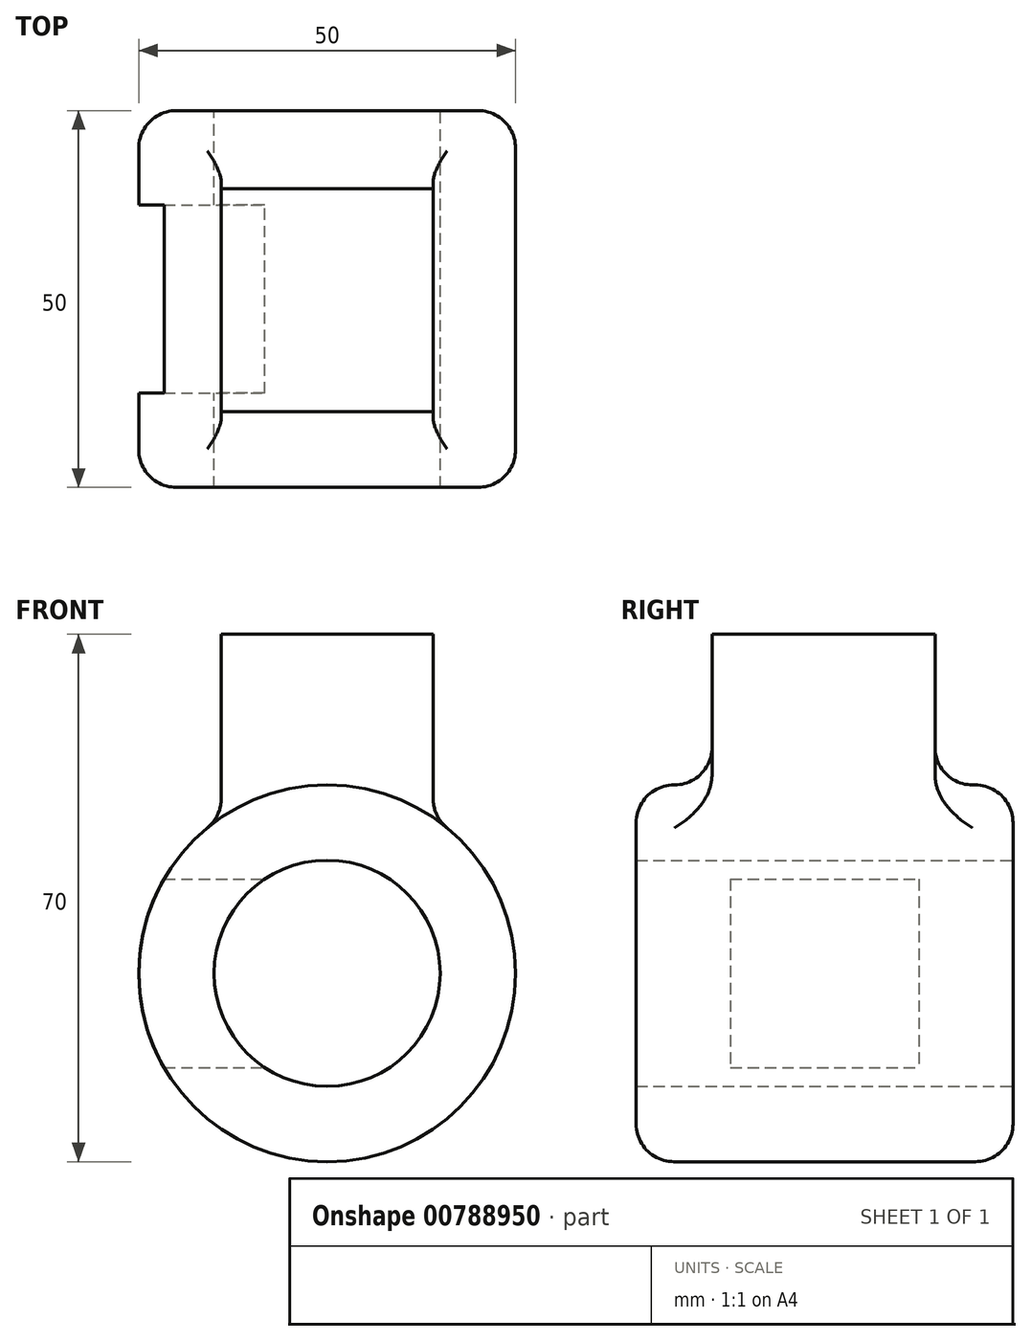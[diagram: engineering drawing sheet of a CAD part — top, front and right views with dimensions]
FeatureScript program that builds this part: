
annotation { "Feature Type Name" : "Feature", "Feature Type Description" : "" }
export const myFeature = defineFeature(function(context is Context, id is Id, definition is map)
    precondition{}
    {
        {
            var Q0;
            Q0=qCreatedBy(makeId("Front.planeOp"),FACE);
            var sketch = newSketch(context, id + "F0", { "sketchPlane" : qUnion([Q0])});
            skCircle(sketch, "E0", {"center": v(0, 0) * mm, "radius": 25 * mm});
            skCircle(sketch, "E1", {"center": v(0, 0) * mm, "radius": 15 * mm});
            skSolve(sketch);
        }
        {
            var Q0;
            Q0 = qSketchRegion(id + "F0", true);
            extrude(context, id + "F1", {"entities" : qUnion([Q0]), "depth" : 50 * mm, "offsetDistance" : 25 * mm});
        }
        {
            var Q0;
            Q0=qCreatedBy(makeId("Right.planeOp"),FACE);
            var sketch = newSketch(context, id + "F2", { "sketchPlane" : qUnion([Q0])});
            skLineSegment(sketch, "E2.bottom", {"start": v(-12.5, 12.5) * mm, "end": v(-37.5, 12.5) * mm});
            skLineSegment(sketch, "E2.top", {"start": v(-12.5, -12.5) * mm, "end": v(-37.5, -12.5) * mm});
            skLineSegment(sketch, "E2.left", {"start": v(-12.5, 12.5) * mm, "end": v(-12.5, -12.5) * mm});
            skLineSegment(sketch, "E2.right", {"start": v(-37.5, 12.5) * mm, "end": v(-37.5, -12.5) * mm});
            skPoint(sketch, "E2.middle", {"position": v(-25, 0) * mm});
            skSolve(sketch);
        }
        {
            var Q0;
            Q0 = qSketchRegion(id + "F2", true);
            extrude(context, id + "F3", {"entities" : qUnion([Q0]), "operationType" : NewBodyOperationType.REMOVE, "oppositeDirection" : true, "depth" : 25 * mm, "offsetDistance" : 25 * mm});
        }
        {
            var Q0;
            Q0=qCreatedBy(makeId("Top.planeOp"),FACE);
            cPlane(context, id + "F4", {"entities" : qUnion([Q0]), "cplaneType" : CPlaneType.OFFSET, "offset" : 20 * mm, "width" : 150 * mm, "height" : 150 * mm});
        }
        {
            var Q0;
            Q0=makeQuery(id+"F1.opExtrude","CAP_EDGE",EDGE,{"disambiguationData":[OSD([sQuery(id+"F0.wireOp",EDGE,"E0")])],"isStart":false});
            var Q1;
            Q1=makeQuery(id+"F1.opExtrude","CAP_EDGE",EDGE,{"disambiguationData":[OSD([sQuery(id+"F0.wireOp",EDGE,"E0")])],"isStart":true});
            fillet(context, id + "F5", {"entities" : qUnion([Q0, Q1]), "radius" : 5 * mm, "tangentPropagation" : true, "allowEdgeOverflow" : false});
        }
        {
            var Q0;
            Q0=qCreatedBy(id+"F4.planeOp",FACE);
            var sketch = newSketch(context, id + "F6", { "sketchPlane" : qUnion([Q0])});
            skLineSegment(sketch, "E3.bottom", {"start": v(14.07, -39.93) * mm, "end": v(-14.07, -39.93) * mm});
            skLineSegment(sketch, "E3.top", {"start": v(14.07, -10.34) * mm, "end": v(-14.07, -10.34) * mm});
            skLineSegment(sketch, "E3.left", {"start": v(14.07, -39.93) * mm, "end": v(14.07, -10.34) * mm});
            skLineSegment(sketch, "E3.right", {"start": v(-14.07, -39.93) * mm, "end": v(-14.07, -10.34) * mm});
            skPoint(sketch, "E3.middle", {"position": v(0, -25.14) * mm});
            skSolve(sketch);
        }
        {
            var Q0;
            Q0 = qSketchRegion(id + "F6", true);
            extrude(context, id + "F7", {"entities" : qUnion([Q0]), "operationType" : NewBodyOperationType.ADD, "depth" : 25 * mm, "offsetDistance" : 25 * mm});
        }
        {
            var Q0;
            Q0=makeQuery(id+"F7.boolean.opBoolean","INTERSECT",EDGE,{"derivedFrom":[makeQuery(id+"F1.opExtrude","SWEPT_FACE",FACE,{"disambiguationData":[OSD([sQuery(id+"F0.wireOp",EDGE,"E0")])]}),makeQuery(id+"F7.opExtrude","SWEPT_FACE",FACE,{"disambiguationData":[OSD([sQuery(id+"F6.wireOp",EDGE,"E3.right")])]})]});
            var Q1;
            Q1=makeQuery(id+"F7.boolean.opBoolean","INTERSECT",EDGE,{"derivedFrom":[makeQuery(id+"F1.opExtrude","SWEPT_FACE",FACE,{"disambiguationData":[OSD([sQuery(id+"F0.wireOp",EDGE,"E0")])]}),makeQuery(id+"F7.opExtrude","SWEPT_FACE",FACE,{"disambiguationData":[OSD([sQuery(id+"F6.wireOp",EDGE,"E3.top")])]})]});
            var Q2;
            Q2=makeQuery(id+"F7.boolean.opBoolean","INTERSECT",EDGE,{"derivedFrom":[makeQuery(id+"F1.opExtrude","SWEPT_FACE",FACE,{"disambiguationData":[OSD([sQuery(id+"F0.wireOp",EDGE,"E0")])]}),makeQuery(id+"F7.opExtrude","SWEPT_FACE",FACE,{"disambiguationData":[OSD([sQuery(id+"F6.wireOp",EDGE,"E3.left")])]})]});
            var Q3;
            Q3=makeQuery(id+"F7.boolean.opBoolean","INTERSECT",EDGE,{"derivedFrom":[makeQuery(id+"F1.opExtrude","SWEPT_FACE",FACE,{"disambiguationData":[OSD([sQuery(id+"F0.wireOp",EDGE,"E0")])]}),makeQuery(id+"F7.opExtrude","SWEPT_FACE",FACE,{"disambiguationData":[OSD([sQuery(id+"F6.wireOp",EDGE,"E3.bottom")])]})]});
            fillet(context, id + "F8", {"entities" : qUnion([Q0, Q1, Q2, Q3]), "radius" : 5 * mm, "tangentPropagation" : true, "allowEdgeOverflow" : false});
        }
    });
